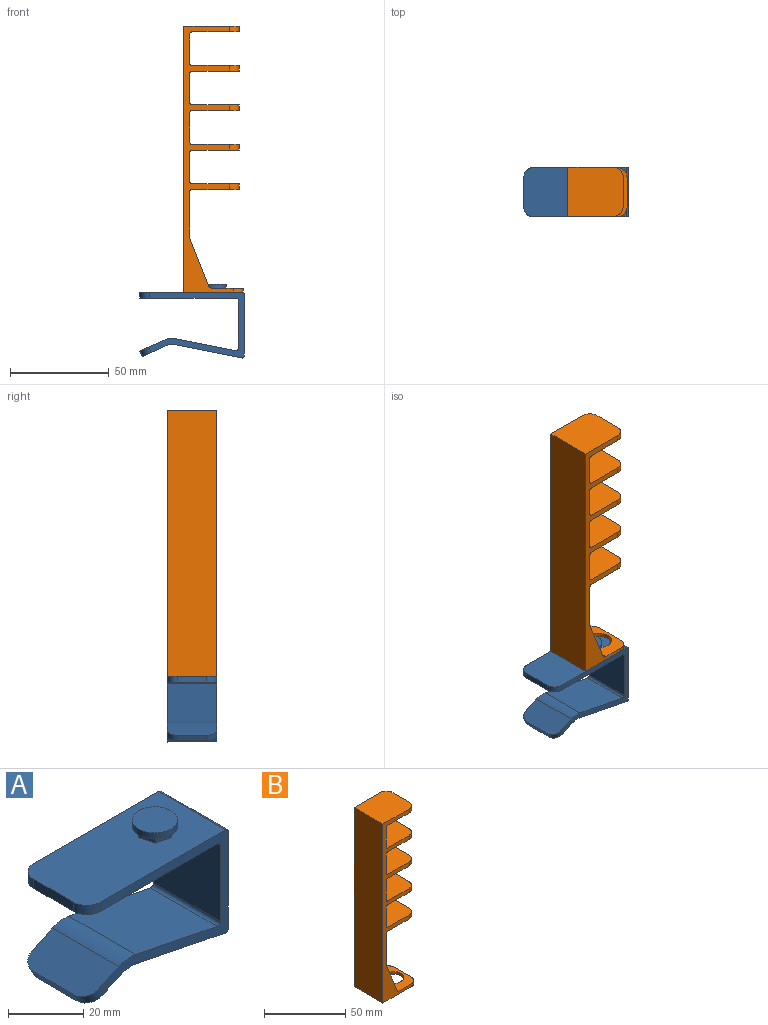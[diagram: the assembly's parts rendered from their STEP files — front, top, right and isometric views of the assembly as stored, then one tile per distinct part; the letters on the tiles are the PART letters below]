
ASSEMBLY  parts=2 mates=1
PART A: 31 faces, bbox 53x25x37.4 mm
  f0: plane 52x25mm, normal (0,0,1), area 1224.3mm2, adj f3,f10,f11,f14,f15,f16,f17,f18
  f1: plane 33.21x25mm, normal (-0.2,0,-0.98), area 846.7mm2, adj f10,f11,f13,f29
  f2: plane 31.44x25mm, normal (1,0,0), area 786mm2, adj f10,f11,f29,f30
  f3: plane 15x3mm, normal (-1,0,0), area 45mm2, adj f0,f4,f21,f23
  f4: plane 49x25mm, normal (0,0,-1), area 1214.3mm2, adj f3,f10,f11,f21,f23,f28
  f5: plane 25x24.78mm, normal (-1,0,0), area 619.5mm2, adj f10,f11,f27,f28
  f6: plane 30.59x25mm, normal (0.2,0,0.98), area 779.8mm2, adj f10,f11,f12,f27
  f7: plane 25x12.03mm, normal (-0.42,0,0.91), area 321.1mm2, adj f8,f10,f11,f12,f20,f22
  f8: plane 15x2.72mm, normal (-0.91,0,-0.42), area 45mm2, adj f7,f9,f20,f22
  f9: plane 25x11.14mm, normal (0.42,0,-0.91), area 296.5mm2, adj f8,f10,f11,f13,f20,f22
  f10: plane 48.47x33.44mm, normal (0,-1,0), area 374.8mm2, adj f0,f1,f2,f4,f5,f6,f7,f9
  f11: plane 48.47x33.44mm, normal (0,1,0), area 374.8mm2, adj f0,f1,f2,f4,f5,f6,f7,f9
  f12: cylinder r=10mm len=25mm, axis (0,1,0), area 158.5mm2, adj f6,f7,f10,f11
  f13: cylinder r=10mm len=25mm, axis (0,-1,0), area 158.5mm2, adj f1,f9,f10,f11
  f14: plane 3.64x3.42mm, normal (-0.73,0.68,0), area 10mm2, adj f0,f15,f19,f24
  f15: plane 4.79x2mm, normal (-0.96,-0.29,0), area 10mm2, adj f0,f14,f16,f24
  f16: plane 4.87x2mm, normal (-0.23,-0.97,0), area 10mm2, adj f0,f15,f17,f24
  f17: plane 3.64x3.42mm, normal (0.73,-0.68,0), area 10mm2, adj f0,f16,f18,f24
  f18: plane 4.79x2mm, normal (0.96,0.29,0), area 10mm2, adj f0,f17,f19,f24
  f19: plane 4.87x2mm, normal (0.23,0.97,0), area 10mm2, adj f0,f14,f18,f24
  f20: cylinder r=5mm len=5.8mm, axis (0.42,0,-0.91), area 23.6mm2, adj f7,f8,f9,f11
  f21: cylinder r=5mm len=5mm, axis (0,0,-1), area 23.6mm2, adj f0,f3,f4,f11
  f22: cylinder r=5mm len=5.8mm, axis (-0.42,0,0.91), area 23.6mm2, adj f7,f8,f9,f10
  f23: cylinder r=5mm len=5mm, axis (0,0,1), area 23.6mm2, adj f0,f3,f4,f10
  f24: plane 12x12mm, normal (0,0,-1), area 48.1mm2, adj f14,f15,f16,f17,f18,f19,f25
  f25: cylinder r=6mm len=12mm, axis (0,0,-1), area 75.4mm2, adj f24,f26
  f26: plane 12x12mm, normal (0,0,1), area 113.1mm2, adj f25
  f27: cylinder r=1mm len=25mm, axis (0,1,0), area 44.2mm2, adj f5,f6,f10,f11
  f28: cylinder r=1mm len=25mm, axis (0,-1,0), area 39.3mm2, adj f4,f5,f10,f11
  f29: cylinder r=1mm len=25mm, axis (0,-1,0), area 44.2mm2, adj f1,f2,f10,f11
  f30: cylinder r=1mm len=25mm, axis (0,1,0), area 39.3mm2, adj f0,f2,f10,f11
PART B: 60 faces, bbox 30x25x135 mm
  f0: plane 23.39x9.35mm, normal (0.93,0,0.37), area 63mm2, adj f12,f54,f56,f57
  f1: plane 25x15mm, normal (1,0,0), area 375mm2, adj f11,f12,f32,f34
  f2: plane 25x15mm, normal (1,0,0), area 375mm2, adj f11,f12,f33,f36
  f3: plane 25x15mm, normal (1,0,0), area 375mm2, adj f11,f12,f35,f38
  f4: plane 25x15mm, normal (1,0,0), area 375mm2, adj f11,f12,f37,f40
  f5: plane 49x25mm, normal (1,0,0), area 1098.1mm2, adj f9,f11,f12,f39,f54,f55,f56,f59
  f6: plane 135x25mm, normal (-1,0,0), area 3375mm2, adj f7,f10,f11,f12
  f7: plane 30x25mm, normal (0,0,-1), area 573.5mm2, adj f6,f8,f11,f12,f13,f14,f15,f16
  f8: plane 15x2mm, normal (1,0,0), area 30mm2, adj f7,f9,f51,f52
  f9: plane 27x25mm, normal (0,0,1), area 441.8mm2, adj f5,f8,f11,f12,f13,f14,f15,f16
  f10: plane 28x25mm, normal (0,0,1), area 689.3mm2, adj f6,f11,f12,f31,f41,f42
  f11: plane 135x25mm, normal (0,-1,0), area 876.3mm2, adj f1,f2,f3,f4,f5,f6,f7,f9
  f12: plane 135x25mm, normal (0,1,0), area 876.3mm2, adj f0,f1,f2,f3,f4,f5,f6,f7
  f13: plane 4.95x2mm, normal (0,1,0), area 9.9mm2, adj f7,f9,f14,f17
  f14: plane 4.29x2.48mm, normal (0.87,0.5,0), area 9.9mm2, adj f7,f9,f13,f15
  f15: plane 4.29x2.48mm, normal (0.87,-0.5,0), area 9.9mm2, adj f7,f9,f14,f16
  f16: plane 4.95x2mm, normal (0,-1,0), area 9.9mm2, adj f7,f9,f15,f17
  f17: cylinder r=6.25mm len=12.5mm, axis (0,0,-1), area 59.6mm2, adj f7,f9,f13,f16
  f18: plane 25x24mm, normal (0,0,-1), area 589.3mm2, adj f11,f12,f20,f39,f49,f50
  f19: plane 25x24mm, normal (0,0,1), area 589.3mm2, adj f11,f12,f20,f40,f49,f50
  f20: plane 15x3mm, normal (1,0,0), area 45mm2, adj f18,f19,f49,f50
  f21: plane 25x24mm, normal (0,0,-1), area 589.3mm2, adj f11,f12,f23,f37,f47,f48
  f22: plane 25x24mm, normal (0,0,1), area 589.3mm2, adj f11,f12,f23,f38,f47,f48
  f23: plane 15x3mm, normal (1,0,0), area 45mm2, adj f21,f22,f47,f48
  f24: plane 25x24mm, normal (0,0,-1), area 589.3mm2, adj f11,f12,f26,f35,f45,f46
  f25: plane 25x24mm, normal (0,0,1), area 589.3mm2, adj f11,f12,f26,f36,f45,f46
  f26: plane 15x3mm, normal (1,0,0), area 45mm2, adj f24,f25,f45,f46
  f27: plane 25x24mm, normal (0,0,-1), area 589.3mm2, adj f11,f12,f29,f33,f43,f44
  f28: plane 25x24mm, normal (0,0,1), area 589.3mm2, adj f11,f12,f29,f34,f43,f44
  f29: plane 15x3mm, normal (1,0,0), area 45mm2, adj f27,f28,f43,f44
  f30: plane 25x24mm, normal (0,0,-1), area 589.3mm2, adj f11,f12,f31,f32,f41,f42
  f31: plane 15x3mm, normal (1,0,0), area 45mm2, adj f10,f30,f41,f42
  f32: cylinder r=1mm len=25mm, axis (0,-1,0), area 39.3mm2, adj f1,f11,f12,f30
  f33: cylinder r=1mm len=25mm, axis (0,-1,0), area 39.3mm2, adj f2,f11,f12,f27
  f34: cylinder r=1mm len=25mm, axis (0,1,0), area 39.3mm2, adj f1,f11,f12,f28
  f35: cylinder r=1mm len=25mm, axis (0,-1,0), area 39.3mm2, adj f3,f11,f12,f24
  f36: cylinder r=1mm len=25mm, axis (0,1,0), area 39.3mm2, adj f2,f11,f12,f25
  f37: cylinder r=1mm len=25mm, axis (0,-1,0), area 39.3mm2, adj f4,f11,f12,f21
  f38: cylinder r=1mm len=25mm, axis (0,1,0), area 39.3mm2, adj f3,f11,f12,f22
  f39: cylinder r=1mm len=25mm, axis (0,-1,0), area 39.3mm2, adj f5,f11,f12,f18
  f40: cylinder r=1mm len=25mm, axis (0,1,0), area 39.3mm2, adj f4,f11,f12,f19
  f41: cylinder r=5mm len=5mm, axis (0,0,-1), area 23.6mm2, adj f10,f12,f30,f31
  f42: cylinder r=5mm len=5mm, axis (0,0,1), area 23.6mm2, adj f10,f11,f30,f31
  f43: cylinder r=5mm len=5mm, axis (0,0,-1), area 23.6mm2, adj f12,f27,f28,f29
  f44: cylinder r=5mm len=5mm, axis (0,0,1), area 23.6mm2, adj f11,f27,f28,f29
  f45: cylinder r=5mm len=5mm, axis (0,0,-1), area 23.6mm2, adj f12,f24,f25,f26
  f46: cylinder r=5mm len=5mm, axis (0,0,1), area 23.6mm2, adj f11,f24,f25,f26
  f47: cylinder r=5mm len=5mm, axis (0,0,-1), area 23.6mm2, adj f12,f21,f22,f23
  f48: cylinder r=5mm len=5mm, axis (0,0,1), area 23.6mm2, adj f11,f21,f22,f23
  f49: cylinder r=5mm len=5mm, axis (0,0,-1), area 23.6mm2, adj f12,f18,f19,f20
  f50: cylinder r=5mm len=5mm, axis (0,0,1), area 23.6mm2, adj f11,f18,f19,f20
  f51: cylinder r=5mm len=5mm, axis (0,0,1), area 15.7mm2, adj f7,f8,f9,f12
  f52: cylinder r=5mm len=5mm, axis (0,0,-1), area 15.7mm2, adj f7,f8,f9,f11
  f53: plane 23.39x9.35mm, normal (0.93,0,0.37), area 63mm2, adj f11,f55,f58,f59
  f54: plane 25.39x11.35mm, normal (0,-1,0), area 125.3mm2, adj f0,f5,f9,f56,f57
  f55: plane 25.39x11.35mm, normal (0,1,0), area 125.3mm2, adj f5,f9,f53,f58,f59
  f56: cylinder r=2mm len=2.5mm, axis (0,1,0), area 1.9mm2, adj f0,f5,f12,f54
  f57: cylinder r=2mm len=2.5mm, axis (0,-1,0), area 6mm2, adj f0,f9,f12,f54
  f58: cylinder r=2mm len=2.5mm, axis (0,-1,0), area 6mm2, adj f9,f11,f53,f55
  f59: cylinder r=2mm len=2.5mm, axis (0,1,0), area 1.9mm2, adj f5,f11,f53,f55
PLACE A t=(-1.71,3.61,15.31)mm
PLACE B t=(-29.31,3.61,31.81)mm
MATE planar B.f7 <-> A.f0  axis (0,0,-1) through (-19.26,-8.89,31.81)mm
